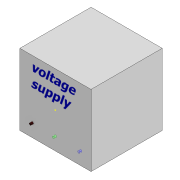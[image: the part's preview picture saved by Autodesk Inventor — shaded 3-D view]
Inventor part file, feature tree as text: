
AUTODESK INVENTOR PART (.ipt)
format: ipt  version: 2021 (Build 250183000, 183)  size: 103,936 bytes
history: native  units: mm
features: other x5, sketch x5, extrude x4
ambient origin geometry x8: Origin, YZ Plane, XZ Plane, XY Plane, X Axis, Y Axis, Z Axis, Center Point
bodies: Body1 (feature_tree), Body2 (feature_tree), Body3 (feature_tree), Body4 (feature_tree)
feature tree (14):
  other  "Твердое тело1"
  extrude  "Выдавливание1"  Depth=10.0mm
  sketch  "Эскиз2"
  other  "РабПлоскость1"
  extrude  "Выдавливание2"  Depth=10.0mm
  extrude  "Выдавливание3"  Depth=10.0mm TaperAngle=0.0deg
  extrude  "Выдавливание4"  TaperAngle=0.0deg  [1 undecoded]
  sketch  "Эскиз1"
  sketch  "Эскиз3"
  other  "Твердое тело2"
  sketch  "Эскиз4"
  other  "Твердое тело3"
  sketch  "Эскиз5"
  other  "Твердое тело4"
note: 1 required parameter value undecoded (feature->parameter linkage not recoverable at this tier; creation-order binding heuristic only, values carry confidence <= 0.55)
